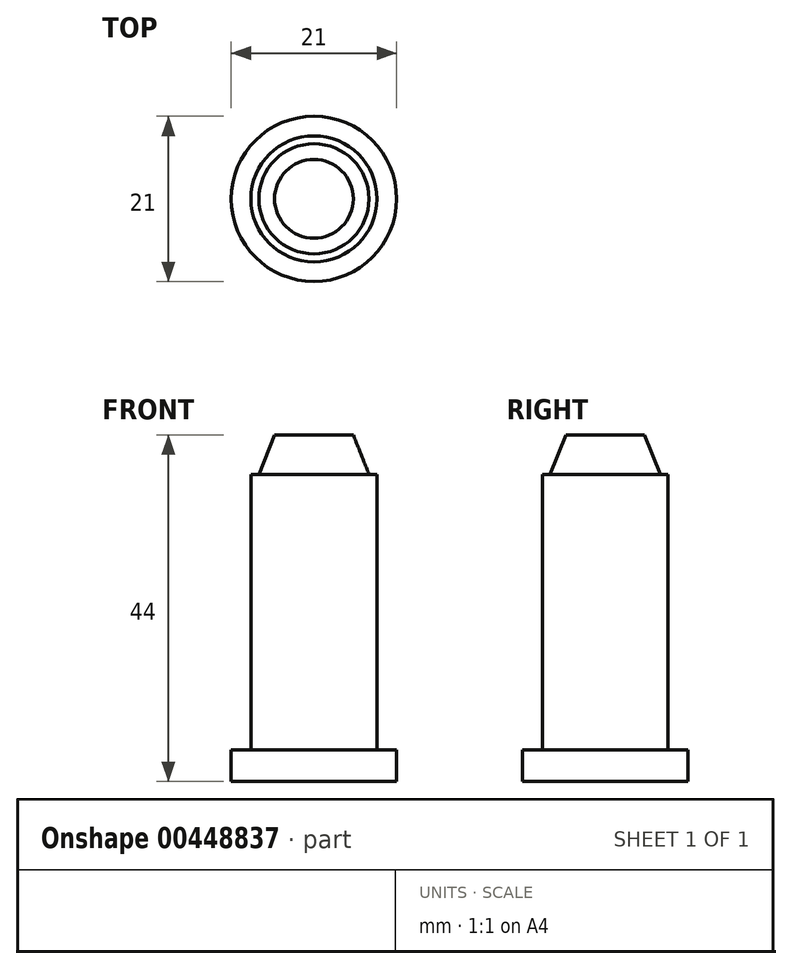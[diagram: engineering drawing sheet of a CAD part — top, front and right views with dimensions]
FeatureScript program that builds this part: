
annotation { "Feature Type Name" : "Feature", "Feature Type Description" : "" }
export const myFeature = defineFeature(function(context is Context, id is Id, definition is map)
    precondition{}
    {
        {
            var Q0;
            Q0=qCreatedBy(makeId("Top.planeOp"),FACE);
            var sketch = newSketch(context, id + "F0", { "sketchPlane" : qUnion([Q0])});
            skCircle(sketch, "E0", {"center": v(0, 0) * mm, "radius": 10.5 * mm});
            skSolve(sketch);
        }
        {
            var Q0;
            Q0=qSketchRegion(id+"F0",true);
            extrude(context, id + "F1", {"entities" : qUnion([Q0]), "depth" : 4 * mm});
        }
        {
            var Q0;
            Q0=qCreatedBy(makeId("Top.planeOp"),FACE);
            var sketch = newSketch(context, id + "F2", { "sketchPlane" : qUnion([Q0])});
            skCircle(sketch, "E1", {"center": v(0, 0) * mm, "radius": 8 * mm});
            skSolve(sketch);
        }
        {
            var Q0;
            Q0=qSketchRegion(id+"F2",true);
            extrude(context, id + "F3", {"entities" : qUnion([Q0]), "operationType" : NewBodyOperationType.ADD, "depth" : 39 * mm});
        }
        {
            var Q0;
            Q0=qCreatedBy(makeId("Right.planeOp"),FACE);
            var sketch = newSketch(context, id + "F4", { "sketchPlane" : qUnion([Q0])});
            skLineSegment(sketch, "E2", {"start": v(0, 44) * mm, "end": v(0, 39) * mm});
            skLineSegment(sketch, "E3", {"start": v(0, 39) * mm, "end": v(7, 39) * mm});
            skLineSegment(sketch, "E4", {"start": v(7, 39) * mm, "end": v(5, 44) * mm});
            skLineSegment(sketch, "E5", {"start": v(5, 44) * mm, "end": v(0, 44) * mm});
            skSolve(sketch);
        }
        {
            var Q0;
            Q0=makeQuery(id+"F4.imprint","IMPRINT",FACE,{"disambiguationData":[TD([[makeQuery(id+"F4.imprint","IMPRINT",EDGE,{"derivedFrom":sQuery(id+"F4.wireOp",EDGE,"E2")}),1.0]])]});
            var Q1;
            Q1=sQuery(id+"F4.wireOp",EDGE,"E2");
            revolve(context, id + "F5", {"operationType" : NewBodyOperationType.ADD, "entities" : qUnion([Q0]), "axis" : qUnion([Q1]), "revolveType" : RevolveType.FULL});
        }
    });
